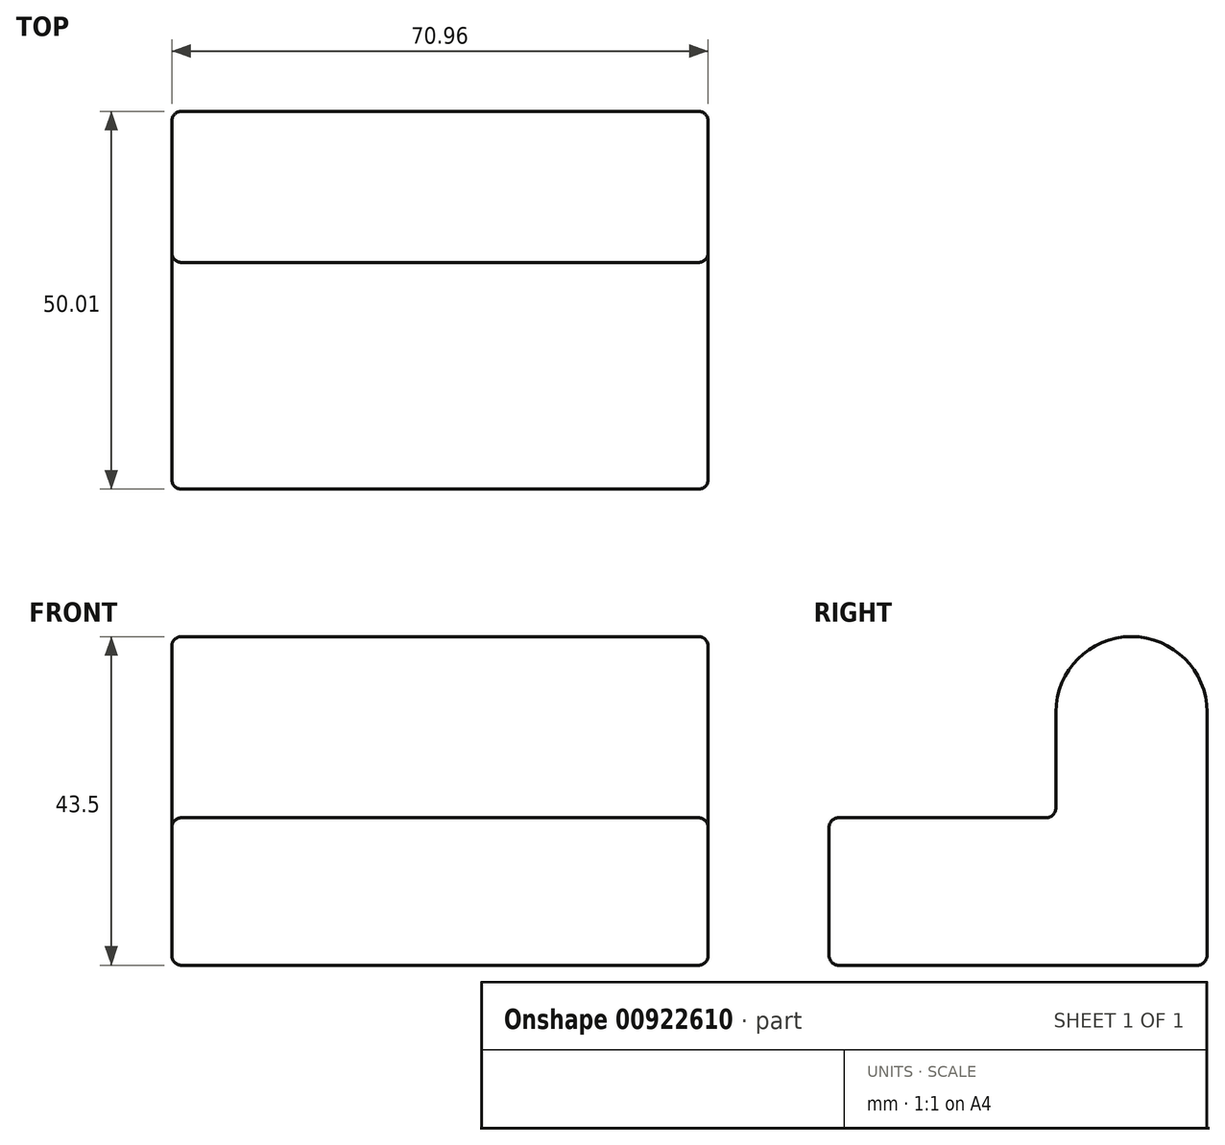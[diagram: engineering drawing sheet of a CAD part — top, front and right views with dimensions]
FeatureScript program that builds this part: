
annotation { "Feature Type Name" : "Feature", "Feature Type Description" : "" }
export const myFeature = defineFeature(function(context is Context, id is Id, definition is map)
    precondition{}
    {
        {
            var Q0;
            Q0=qCreatedBy(makeId("Right.planeOp"),FACE);
            var sketch = newSketch(context, id + "F0", { "sketchPlane" : qUnion([Q0])});
            skLineSegment(sketch, "E0", {"start": v(0, 0) * mm, "end": v(-1000.13, 0) * mm});
            skLineSegment(sketch, "E1", {"start": v(-1000.13, 0) * mm, "end": v(-1000.13, 390.53) * mm});
            skLineSegment(sketch, "E2", {"start": v(-1000.13, 390.53) * mm, "end": v(-400.05, 390.53) * mm});
            skLineSegment(sketch, "E3", {"start": v(-400.05, 390.52) * mm, "end": v(-400.05, 669.93) * mm});
            skLineSegment(sketch, "E4", {"start": v(0, 0) * mm, "end": v(0, 669.93) * mm});
            skLineSegment(sketch, "E5", {"start": v(-400.05, 669.93) * mm, "end": v(0, 669.93) * mm, "construction": true});
            skArc(sketch, "E6", {"start": v(-400.05, 669.93) * mm, "mid": v(-200.02, 869.95) * mm, "end": v(0, 669.93) * mm});
            skSolve(sketch);
        }
        {
            var Q0;
            Q0 = qSketchRegion(id + "F0", true);
            extrude(context, id + "F1", {"entities" : qUnion([Q0]), "endBound" : BoundingType.SYMMETRIC, "depth" : 1419.22 * mm, "offsetDistance" : 25.4 * mm});
        }
        {
            var Q0;
            Q0=makeQuery(id+"F1.opExtrude","CAP_EDGE",EDGE,{"disambiguationData":[OSD([sQuery(id+"F0.wireOp",EDGE,"E4")])],"isStart":false});
            var Q1;
            Q1=makeQuery(id+"F1.opExtrude","SWEPT_FACE",FACE,{"disambiguationData":[OSD([sQuery(id+"F0.wireOp",EDGE,"E0")])]});
            var Q2;
            Q2=makeQuery(id+"F1.opExtrude","SWEPT_EDGE",EDGE,{"disambiguationData":[OSD([sQuery(id+"F0.wireOp",EDGE,"E0"),sQuery(id+"F0.wireOp",EDGE,"E1")])]});
            var Q3;
            Q3=makeQuery(id+"F1.opExtrude","CAP_FACE",FACE,{"disambiguationData":[OSD([sQuery(id+"F0.wireOp",EDGE,"E0"),sQuery(id+"F0.wireOp",EDGE,"E1"),sQuery(id+"F0.wireOp",EDGE,"E2"),sQuery(id+"F0.wireOp",EDGE,"E3"),sQuery(id+"F0.wireOp",EDGE,"E4"),sQuery(id+"F0.wireOp",EDGE,"E6")])],"isStart":true});
            var Q4;
            Q4=makeQuery(id+"F1.opExtrude","SWEPT_EDGE",EDGE,{"disambiguationData":[OSD([sQuery(id+"F0.wireOp",EDGE,"E1"),sQuery(id+"F0.wireOp",EDGE,"E2")])]});
            var Q5;
            Q5=makeQuery(id+"F1.opExtrude","CAP_FACE",FACE,{"disambiguationData":[OSD([sQuery(id+"F0.wireOp",EDGE,"E0"),sQuery(id+"F0.wireOp",EDGE,"E1"),sQuery(id+"F0.wireOp",EDGE,"E2"),sQuery(id+"F0.wireOp",EDGE,"E3"),sQuery(id+"F0.wireOp",EDGE,"E4"),sQuery(id+"F0.wireOp",EDGE,"E6")])],"isStart":false});
            var Q6;
            Q6=makeQuery(id+"F1.opExtrude","SWEPT_EDGE",EDGE,{"disambiguationData":[OSD([sQuery(id+"F0.wireOp",EDGE,"E2"),sQuery(id+"F0.wireOp",EDGE,"E3")])]});
            var Q7;
            Q7=makeQuery(id+"F1.opExtrude","SWEPT_FACE",FACE,{"disambiguationData":[OSD([sQuery(id+"F0.wireOp",EDGE,"E1")])]});
            var Q8;
            Q8=makeQuery(id+"F1.opExtrude","SWEPT_FACE",FACE,{"disambiguationData":[OSD([sQuery(id+"F0.wireOp",EDGE,"E2")])]});
            var Q9;
            Q9=makeQuery(id+"F1.opExtrude","SWEPT_FACE",FACE,{"disambiguationData":[OSD([sQuery(id+"F0.wireOp",EDGE,"E3")])]});
            var Q10;
            Q10=makeQuery(id+"F1.opExtrude","SWEPT_FACE",FACE,{"disambiguationData":[OSD([sQuery(id+"F0.wireOp",EDGE,"E4")])]});
            var Q11;
            Q11=makeQuery(id+"F1.opExtrude","SWEPT_FACE",FACE,{"disambiguationData":[OSD([sQuery(id+"F0.wireOp",EDGE,"E6")])]});
            var Q12;
            Q12=makeQuery(id+"F1.opExtrude","CAP_EDGE",EDGE,{"disambiguationData":[OSD([sQuery(id+"F0.wireOp",EDGE,"E6")])],"isStart":true});
            var Q13;
            Q13=makeQuery(id+"F1.opExtrude","CAP_EDGE",EDGE,{"disambiguationData":[OSD([sQuery(id+"F0.wireOp",EDGE,"E6")])],"isStart":false});
            var Q14;
            Q14=makeQuery(id+"F1.opExtrude","CAP_EDGE",EDGE,{"disambiguationData":[OSD([sQuery(id+"F0.wireOp",EDGE,"E3")])],"isStart":false});
            var Q15;
            Q15=makeQuery(id+"F1.opExtrude","CAP_EDGE",EDGE,{"disambiguationData":[OSD([sQuery(id+"F0.wireOp",EDGE,"E4")])],"isStart":true});
            var Q16;
            Q16=makeQuery(id+"F1.opExtrude","SWEPT_EDGE",EDGE,{"disambiguationData":[OSD([sQuery(id+"F0.wireOp",EDGE,"E0"),sQuery(id+"F0.wireOp",EDGE,"E4")])]});
            var Q17;
            Q17=makeQuery(id+"F1.opExtrude","SWEPT_EDGE",EDGE,{"disambiguationData":[OSD([sQuery(id+"F0.wireOp",EDGE,"E3"),sQuery(id+"F0.wireOp",EDGE,"E6")])]});
            var Q18;
            Q18=makeQuery(id+"F1.opExtrude","SWEPT_EDGE",EDGE,{"disambiguationData":[OSD([sQuery(id+"F0.wireOp",EDGE,"E4"),sQuery(id+"F0.wireOp",EDGE,"E6")])]});
            var Q19;
            Q19=makeQuery(id+"F1.opExtrude","CAP_EDGE",EDGE,{"disambiguationData":[OSD([sQuery(id+"F0.wireOp",EDGE,"E0")])],"isStart":true});
            var Q20;
            Q20=makeQuery(id+"F1.opExtrude","CAP_EDGE",EDGE,{"disambiguationData":[OSD([sQuery(id+"F0.wireOp",EDGE,"E0")])],"isStart":false});
            var Q21;
            Q21=makeQuery(id+"F1.opExtrude","CAP_EDGE",EDGE,{"disambiguationData":[OSD([sQuery(id+"F0.wireOp",EDGE,"E1")])],"isStart":true});
            var Q22;
            Q22=makeQuery(id+"F1.opExtrude","CAP_EDGE",EDGE,{"disambiguationData":[OSD([sQuery(id+"F0.wireOp",EDGE,"E1")])],"isStart":false});
            var Q23;
            Q23=makeQuery(id+"F1.opExtrude","CAP_EDGE",EDGE,{"disambiguationData":[OSD([sQuery(id+"F0.wireOp",EDGE,"E2")])],"isStart":true});
            var Q24;
            Q24=makeQuery(id+"F1.opExtrude","CAP_EDGE",EDGE,{"disambiguationData":[OSD([sQuery(id+"F0.wireOp",EDGE,"E2")])],"isStart":false});
            var Q25;
            Q25=makeQuery(id+"F1.opExtrude","CAP_EDGE",EDGE,{"disambiguationData":[OSD([sQuery(id+"F0.wireOp",EDGE,"E3")])],"isStart":true});
            fillet(context, id + "F2", {"entities" : qUnion([Q0, Q1, Q2, Q3, Q4, Q5, Q6, Q7, Q8, Q9, Q10, Q11, Q12, Q13, Q14, Q15, Q16, Q17, Q18, Q19, Q20, Q21, Q22, Q23, Q24, Q25]), "radius" : 25.4 * mm, "tangentPropagation" : true, "allowEdgeOverflow" : false});
        }
        {
            var Q0;
            Q0=makeQuery(id+"F1.opExtrude","SWEPT_BODY",BODY,{"disambiguationData":[OSD([sQuery(id+"F0.wireOp",EDGE,"E0"),sQuery(id+"F0.wireOp",EDGE,"E1"),sQuery(id+"F0.wireOp",EDGE,"E2"),sQuery(id+"F0.wireOp",EDGE,"E3"),sQuery(id+"F0.wireOp",EDGE,"E4"),sQuery(id+"F0.wireOp",EDGE,"E6")])]});
            var Q1;
            Q1=qCreatedBy(makeId("Origin.pointOp"),VERTEX);
            transform(context, id + "F3", {"entities" : qUnion([Q0]), "transformType" : TransformType.SCALE_UNIFORMLY, "scale" : 0.05, "scalePoint" : qUnion([Q1]), "makeCopy" : false});
        }
    });
